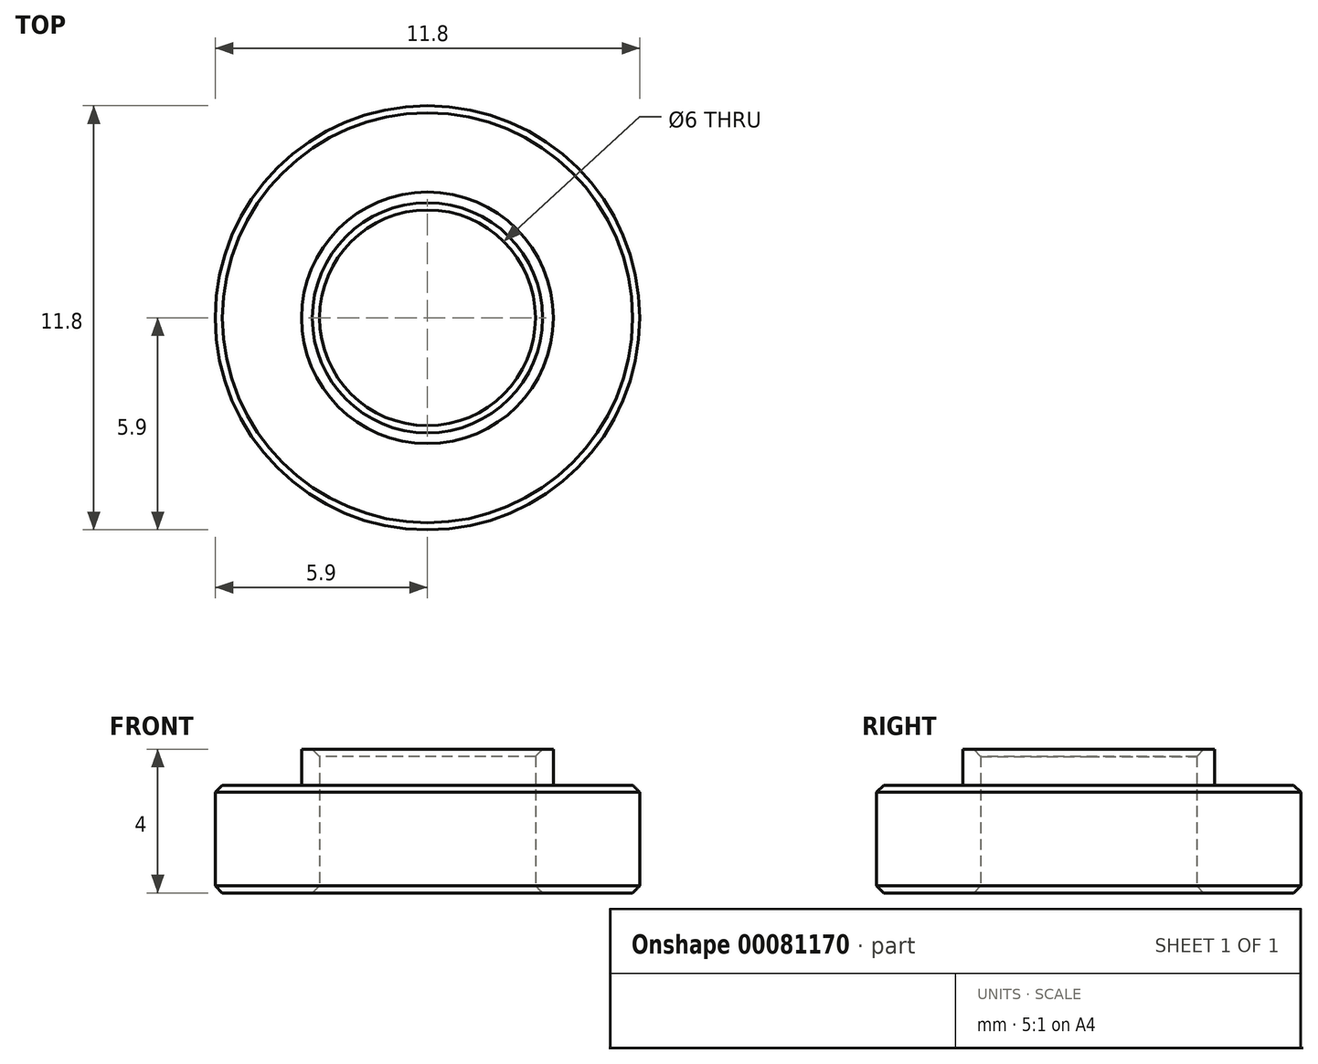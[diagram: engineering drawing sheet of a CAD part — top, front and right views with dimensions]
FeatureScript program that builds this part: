
annotation { "Feature Type Name" : "Feature", "Feature Type Description" : "" }
export const myFeature = defineFeature(function(context is Context, id is Id, definition is map)
    precondition{}
    {
        {
            var Q0;
            Q0=qCreatedBy(makeId("Top.planeOp"),FACE);
            var sketch = newSketch(context, id + "F0", { "sketchPlane" : qUnion([Q0])});
            skCircle(sketch, "E0", {"center": v(0, 0) * mm, "radius": 5.9 * mm});
            skSolve(sketch);
        }
        {
            var Q0;
            Q0=qSketchRegion(id+"F0",true);
            extrude(context, id + "F1", {"entities" : qUnion([Q0]), "depth" : 3 * mm});
        }
        {
            var Q0;
            Q0=makeQuery(id+"F1.opExtrude","CAP_FACE",FACE,{"disambiguationData":[OSD([sQuery(id+"F0.wireOp",EDGE,"E0")])],"isStart":false});
            var sketch = newSketch(context, id + "F2", { "sketchPlane" : qUnion([Q0])});
            skCircle(sketch, "E1", {"center": v(0, 0) * mm, "radius": 3.5 * mm});
            skSolve(sketch);
        }
        {
            var Q0;
            Q0=qSketchRegion(id+"F2",true);
            extrude(context, id + "F3", {"entities" : qUnion([Q0]), "operationType" : NewBodyOperationType.ADD, "depth" : 1 * mm});
        }
        {
            var Q0;
            Q0=makeQuery(id+"F1.opExtrude","CAP_FACE",FACE,{"disambiguationData":[OSD([sQuery(id+"F0.wireOp",EDGE,"E0")])],"isStart":true});
            var sketch = newSketch(context, id + "F4", { "sketchPlane" : qUnion([Q0])});
            skCircle(sketch, "E2", {"center": v(0, 0) * mm, "radius": 3 * mm});
            skSolve(sketch);
        }
        {
            var Q0;
            Q0=qSketchRegion(id+"F4",true);
            extrude(context, id + "F5", {"entities" : qUnion([Q0]), "operationType" : NewBodyOperationType.REMOVE, "endBound" : BoundingType.THROUGH_ALL, "oppositeDirection" : true, "depth" : 25 * mm});
        }
        {
            var Q0;
            Q0=makeQuery(id+"F1.opExtrude","CAP_EDGE",EDGE,{"disambiguationData":[OSD([sQuery(id+"F0.wireOp",EDGE,"E0")])],"isStart":false});
            var Q1;
            Q1=makeQuery(id+"F1.opExtrude","CAP_FACE",FACE,{"disambiguationData":[OSD([sQuery(id+"F0.wireOp",EDGE,"E0")])],"isStart":true});
            var Q2;
            Q2=makeQuery(id+"F5.boolean.opBoolean","INTERSECT",EDGE,{"derivedFrom":[makeQuery(id+"F3.opExtrude","CAP_FACE",FACE,{"disambiguationData":[OSD([sQuery(id+"F2.wireOp",EDGE,"E1")])],"isStart":false}),makeQuery(id+"F5.opExtrude","SWEPT_FACE",FACE,{"disambiguationData":[OSD([sQuery(id+"F4.wireOp",EDGE,"E2")])]})]});
            chamfer(context, id + "F6", {"entities" : qUnion([Q0, Q1, Q2]), "width" : .2 * mm, "tangentPropagation" : true});
        }
    });
